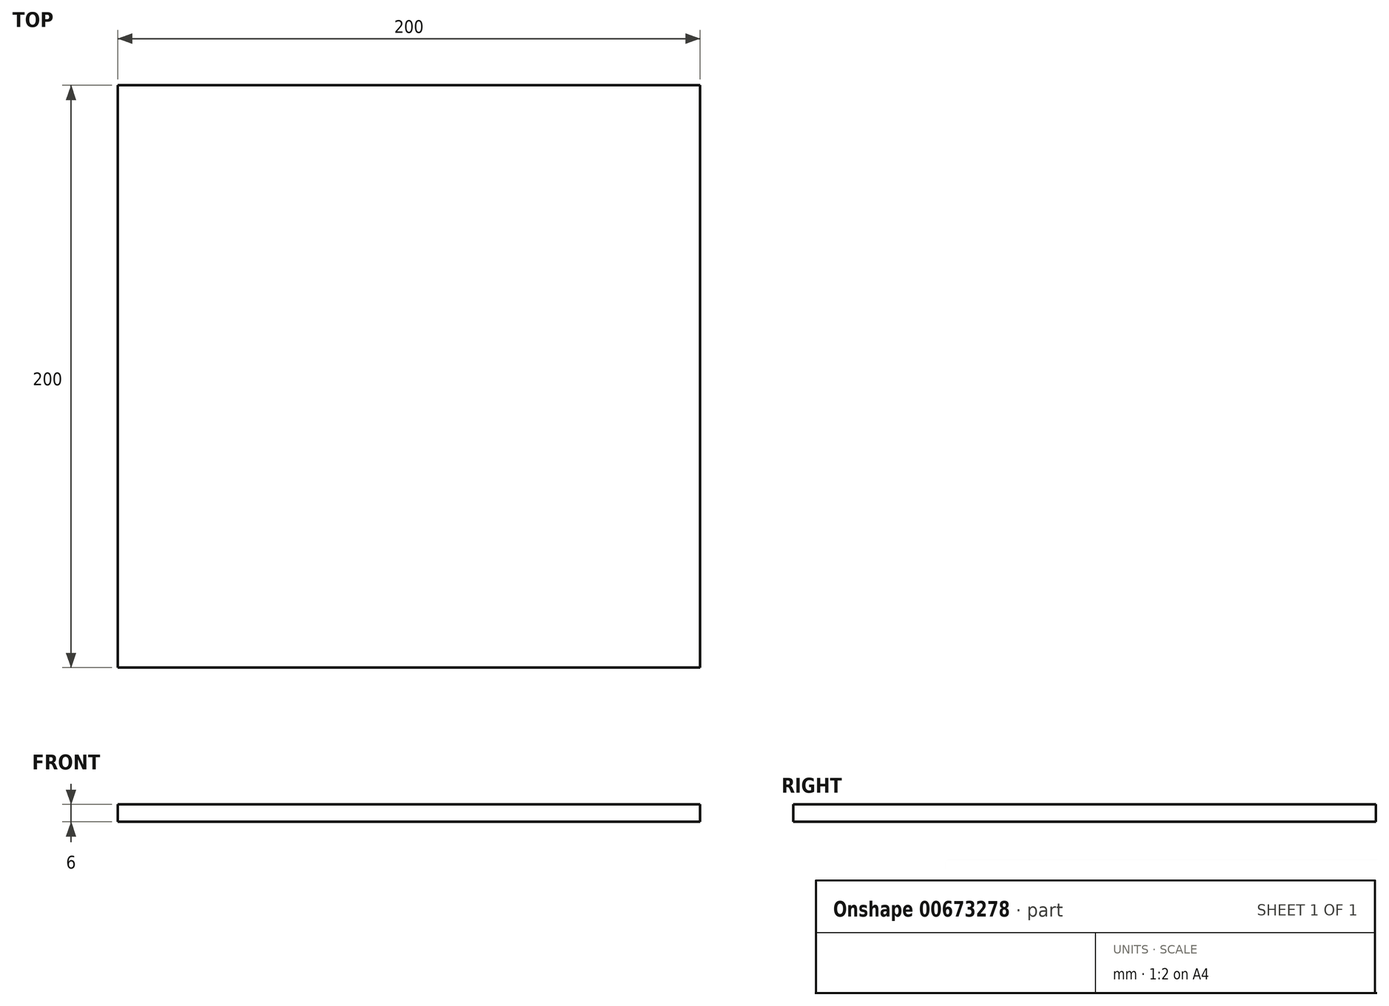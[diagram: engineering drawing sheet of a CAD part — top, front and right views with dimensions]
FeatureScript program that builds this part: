
annotation { "Feature Type Name" : "Feature", "Feature Type Description" : "" }
export const myFeature = defineFeature(function(context is Context, id is Id, definition is map)
    precondition{}
    {
        {
            var Q0;
            Q0=qCreatedBy(makeId("Top.planeOp"),FACE);
            var sketch = newSketch(context, id + "F0", { "sketchPlane" : qUnion([Q0])});
            skLineSegment(sketch, "E0.bottom", {"start": v(0, 200) * mm, "end": v(200, 200) * mm});
            skLineSegment(sketch, "E0.top", {"start": v(0, 0) * mm, "end": v(200, 0) * mm});
            skLineSegment(sketch, "E0.left", {"start": v(0, 200) * mm, "end": v(0, 0) * mm});
            skLineSegment(sketch, "E0.right", {"start": v(200, 200) * mm, "end": v(200, 0) * mm});
            skSolve(sketch);
        }
        {
            var Q0;
            Q0=makeQuery(id+"F0.imprint","IMPRINT",FACE,{"disambiguationData":[TD([[makeQuery(id+"F0.imprint","IMPRINT",EDGE,{"derivedFrom":sQuery(id+"F0.wireOp",EDGE,"E0.bottom")}),-1.0]])]});
            extrude(context, id + "F1", {"entities" : qUnion([Q0]), "depth" : 6 * mm, "offsetDistance" : 25 * mm});
        }
    });
